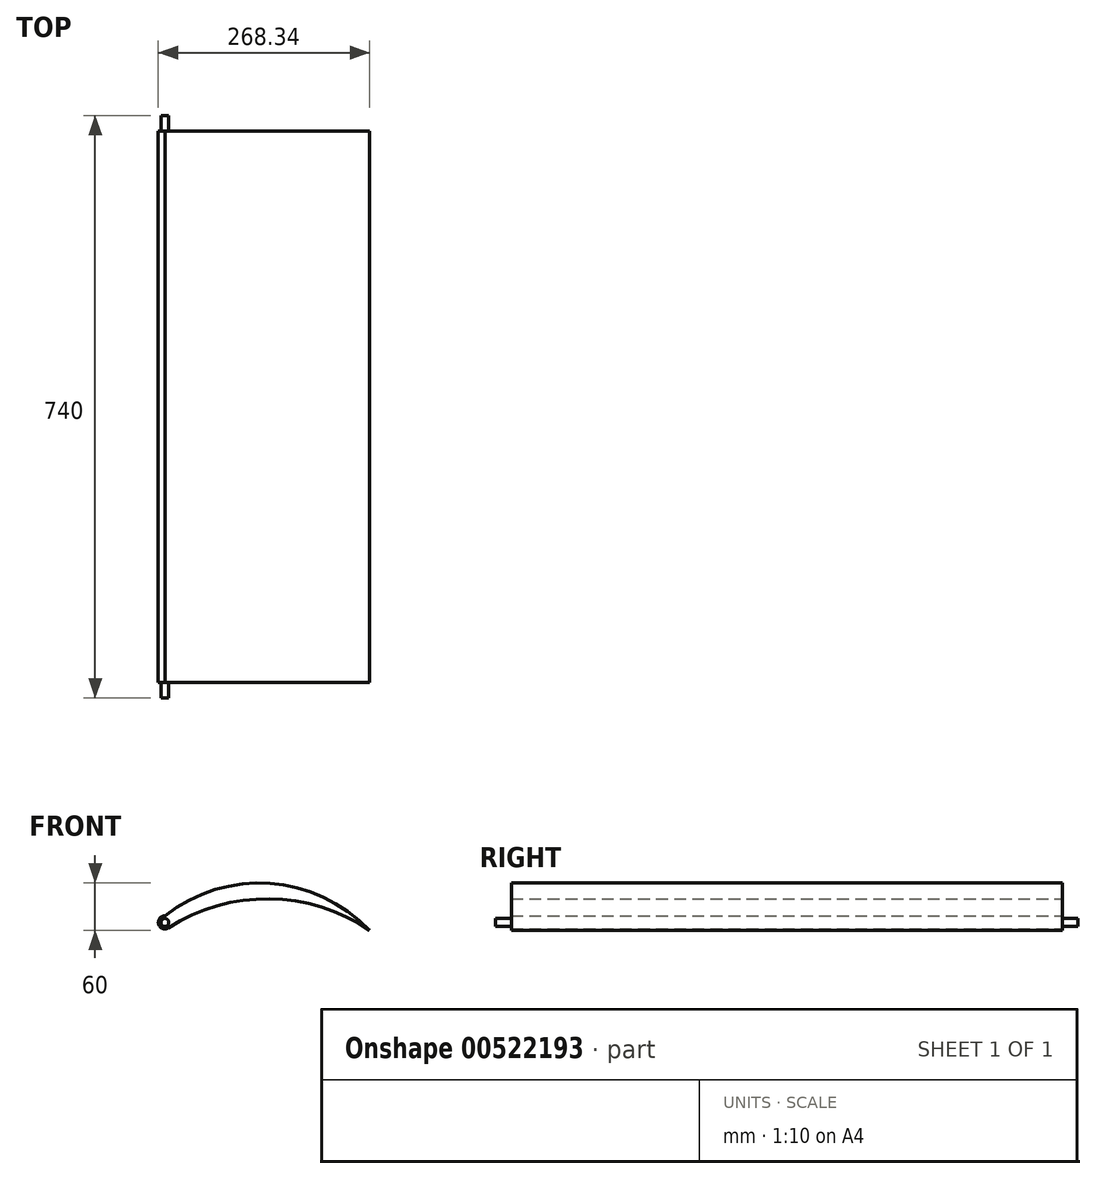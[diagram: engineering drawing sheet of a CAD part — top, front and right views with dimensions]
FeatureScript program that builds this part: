
annotation { "Feature Type Name" : "Feature", "Feature Type Description" : "" }
export const myFeature = defineFeature(function(context is Context, id is Id, definition is map)
    precondition{}
    {
        {
            var Q0;
            Q0=qCreatedBy(makeId("Front.planeOp"),FACE);
            var sketch = newSketch(context, id + "F0", { "sketchPlane" : qUnion([Q0])});
            skLineSegment(sketch, "E0.bottom", {"start": v(0, 0) * mm, "end": v(260, 0) * mm});
            skLineSegment(sketch, "E0.top", {"start": v(0, 100) * mm, "end": v(260, 100) * mm});
            skLineSegment(sketch, "E0.left", {"start": v(0, 0) * mm, "end": v(0, 100) * mm});
            skLineSegment(sketch, "E0.right", {"start": v(260, 0) * mm, "end": v(260, 100) * mm});
            skArc(sketch, "E1", {"start": v(260, 0) * mm, "mid": v(130, 40) * mm, "end": v(0, 0) * mm});
            skCircle(sketch, "E2", {"center": v(0, 10) * mm, "radius": 8.34 * mm});
            skArc(sketch, "E3", {"start": v(260, 0) * mm, "mid": v(133.55, 59.52) * mm, "end": v(0, 18.34) * mm});
            skSolve(sketch);
        }
        {
            var Q0;
            {var subQ0=sQuery(id+"F0.wireOp",EDGE,"E3");Q0=makeQuery(id+"F0.imprint","IMPRINT",FACE,{"disambiguationData":[TD([[makeQuery(id+"F0.imprint","IMPRINT",EDGE,{"derivedFrom":subQ0}),1.0]])]});}
            var Q1;
            {var subQ0=sQuery(id+"F0.wireOp",EDGE,"E2");var subQ1=sQuery(id+"F0.wireOp",EDGE,"E0.left");var subQ3=makeQuery(id+"F0.imprint","INTERSECT",VERTEX,{"derivedFrom":[subQ1,subQ0]});Q1=makeQuery(id+"F0.imprint","IMPRINT",FACE,{"disambiguationData":[TD([[makeQuery(id+"F0.imprint","IMPRINT",EDGE,{"disambiguationData":[TD([[subQ3,-1.0]])],"derivedFrom":subQ0}),1.0]])]});}
            var Q2;
            {var subQ0=sQuery(id+"F0.wireOp",EDGE,"E2");var subQ1=sQuery(id+"F0.wireOp",EDGE,"E0.left");var subQ3=makeQuery(id+"F0.imprint","INTERSECT",VERTEX,{"derivedFrom":[subQ1,subQ0]});Q2=makeQuery(id+"F0.imprint","IMPRINT",FACE,{"disambiguationData":[TD([[makeQuery(id+"F0.imprint","IMPRINT",EDGE,{"disambiguationData":[TD([[subQ3,-1.0]])],"derivedFrom":subQ1}),1.0]])]});}
            extrude(context, id + "F1", {"entities" : qUnion([Q0, Q1, Q2]), "depth" : 700 * mm, "offsetDistance" : 25.4 * mm});
        }
        {
            var Q0;
            Q0=makeQuery(id+"F1.opExtrude","CAP_FACE",FACE,{"disambiguationData":[OSD([sQuery(id+"F0.wireOp",EDGE,"E1"),sQuery(id+"F0.wireOp",EDGE,"E2"),sQuery(id+"F0.wireOp",EDGE,"E3")])],"isStart":false});
            var sketch = newSketch(context, id + "F2", { "sketchPlane" : qUnion([Q0])});
            skCircle(sketch, "E4", {"center": v(0, 10) * mm, "radius": 5 * mm});
            skSolve(sketch);
        }
        {
            var Q0;
            Q0=makeQuery(id+"F2.imprint","IMPRINT",FACE,{"disambiguationData":[TD([[makeQuery(id+"F2.imprint","IMPRINT",EDGE,{"derivedFrom":sQuery(id+"F2.wireOp",EDGE,"E4")}),1.0]])]});
            extrude(context, id + "F3", {"entities" : qUnion([Q0]), "operationType" : NewBodyOperationType.ADD, "depth" : 20 * mm, "offsetDistance" : 25.4 * mm});
        }
        {
            var Q0;
            Q0=makeQuery(id+"F1.opExtrude","CAP_FACE",FACE,{"disambiguationData":[OSD([sQuery(id+"F0.wireOp",EDGE,"E1"),sQuery(id+"F0.wireOp",EDGE,"E2"),sQuery(id+"F0.wireOp",EDGE,"E3")])],"isStart":true});
            var sketch = newSketch(context, id + "F4", { "sketchPlane" : qUnion([Q0])});
            skCircle(sketch, "E5", {"center": v(0, 10) * mm, "radius": 5 * mm});
            skSolve(sketch);
        }
        {
            var Q0;
            Q0=makeQuery(id+"F4.imprint","IMPRINT",FACE,{"disambiguationData":[TD([[makeQuery(id+"F4.imprint","IMPRINT",EDGE,{"derivedFrom":sQuery(id+"F4.wireOp",EDGE,"E5")}),1.0]])]});
            extrude(context, id + "F5", {"entities" : qUnion([Q0]), "operationType" : NewBodyOperationType.ADD, "depth" : 20 * mm, "offsetDistance" : 25.4 * mm});
        }
    });
